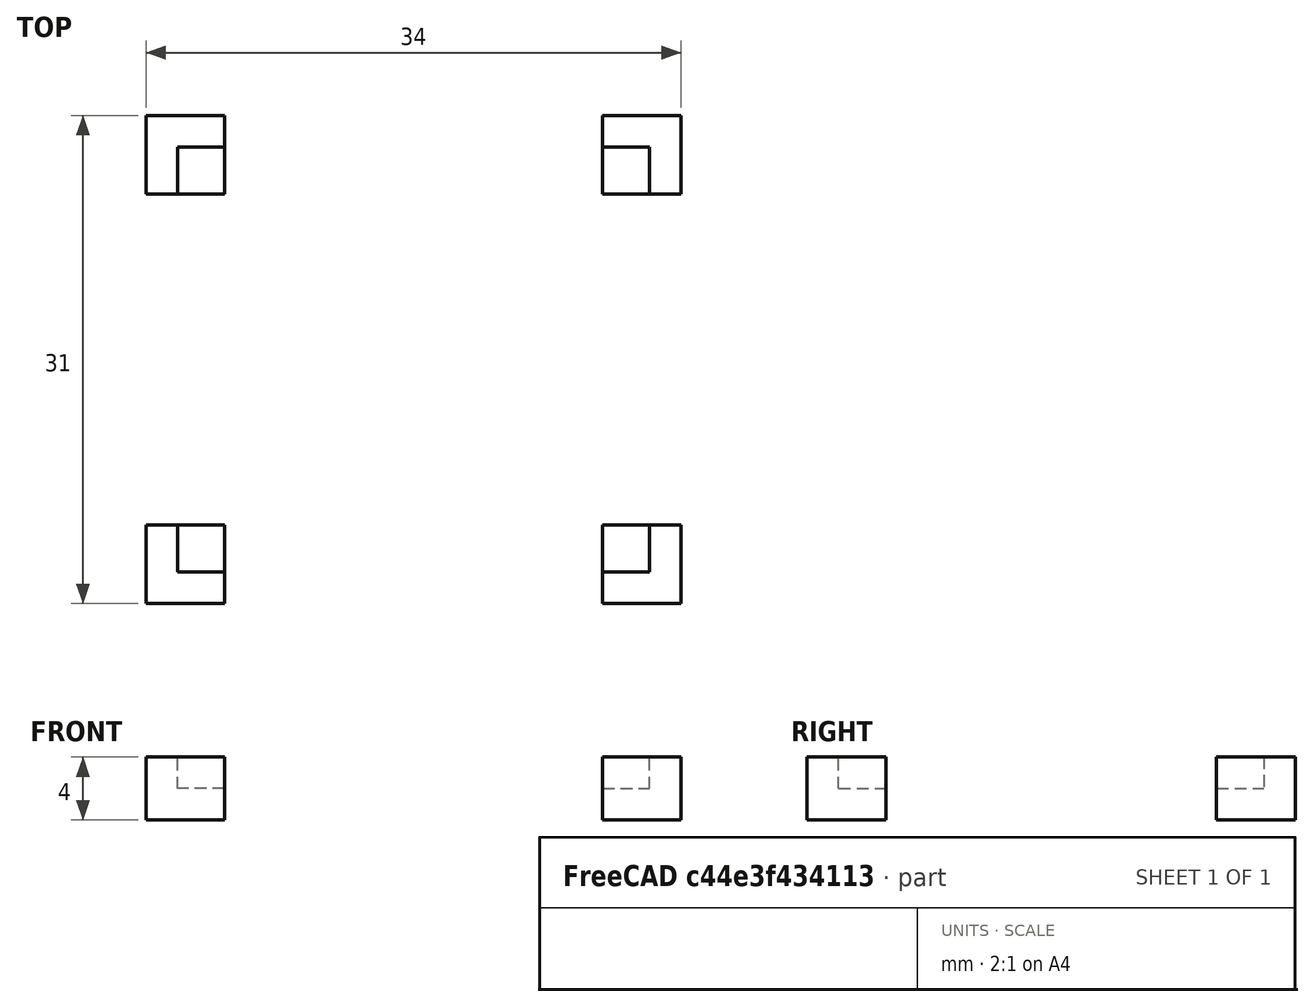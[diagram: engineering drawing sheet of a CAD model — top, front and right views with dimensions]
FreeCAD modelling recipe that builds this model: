
FCSTD DOCUMENT  (FreeCAD 0.16R6712 (Git))
Label: ESP8266_AiThinkerExpansionHolder
License: All rights reserved
LicenseURL: http://en.wikipedia.org/wiki/All_rights_reserved
objects: Part::Box×4, Part::Cut×3, App::DocumentObjectGroup×1
note: 7 computed .brp shape members not serialized (recipe doc carries the construction recipe); baked Part::Feature solids carry a one-line shape summary decoded from their .brp

FEATURE [Part::Box] Box  label="Expansionmodule"
  Height = 3
  Length = 30
  Placement = pos=(2,2,2) rot=(0,0,1;0rad)
  Width = 27
FEATURE [Part::Box] Box001  label="Cube"
  Height = 4
  Length = 34
  Width = 31
FEATURE [Part::Cut] Cut
  Base = -> Box001
  Tool = -> Box
FEATURE [Part::Box] Box002  label="Cube001"
  Height = 10
  Length = 34
  Placement = pos=(0,5,0) rot=(0,0,1;0rad)
  Width = 21
FEATURE [Part::Cut] Cut001
  Base = -> Cut
  Tool = -> Box002
FEATURE [Part::Box] Box003  label="Cube002"
  Height = 10
  Length = 24
  Placement = pos=(5,0,0) rot=(0,0,1;0rad)
  Width = 31
FEATURE [Part::Cut] Cut002
  Base = -> Cut001
  Tool = -> Box003
FEATURE [App::DocumentObjectGroup] Group  label="AiThinkerExpansionHolder"
  Group = -> [Cut002]
